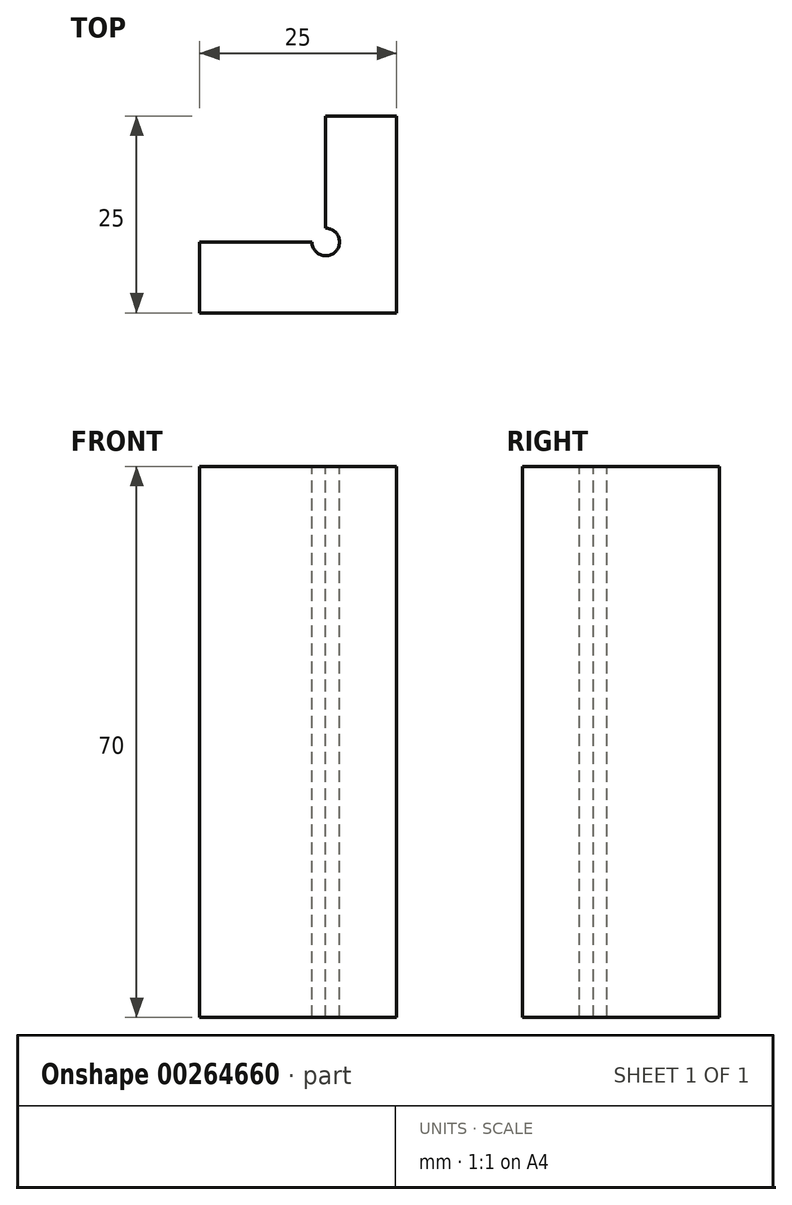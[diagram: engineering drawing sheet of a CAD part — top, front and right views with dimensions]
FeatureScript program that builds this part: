
annotation { "Feature Type Name" : "Feature", "Feature Type Description" : "" }
export const myFeature = defineFeature(function(context is Context, id is Id, definition is map)
    precondition{}
    {
        {
            var Q0;
            Q0=qCreatedBy(makeId("Top.planeOp"),FACE);
            var sketch = newSketch(context, id + "F0", { "sketchPlane" : qUnion([Q0])});
            skLineSegment(sketch, "E0.bottom", {"start": v(3.5, 12.5) * mm, "end": v(12.5, 12.5) * mm});
            skLineSegment(sketch, "E0.top", {"start": v(-12.5, -12.5) * mm, "end": v(12.5, -12.5) * mm});
            skLineSegment(sketch, "E0.left", {"start": v(-12.5, -3.5) * mm, "end": v(-12.5, -12.5) * mm});
            skLineSegment(sketch, "E0.right", {"start": v(12.5, 12.5) * mm, "end": v(12.5, -12.5) * mm});
            skPoint(sketch, "E0.middle", {"position": v(0, 0) * mm});
            skLineSegment(sketch, "E1.top", {"start": v(-12.5, -3.5) * mm, "end": v(1.75, -3.5) * mm});
            skLineSegment(sketch, "E1.right", {"start": v(3.5, 12.5) * mm, "end": v(3.5, -1.75) * mm});
            skPoint(sketch, "E2.orphan", {"position": v(-12.5, 12.5) * mm});
            skArc(sketch, "E3", {"start": v(1.75, -3.5) * mm, "mid": v(4.74, -4.74) * mm, "end": v(3.5, -1.75) * mm});
            skSolve(sketch);
        }
        {
            var Q0;
            Q0 = qSketchRegion(id + "F0", true);
            extrude(context, id + "F1", {"entities" : qUnion([Q0]), "oppositeDirection" : true, "depth" : 70 * mm});
        }
    });
